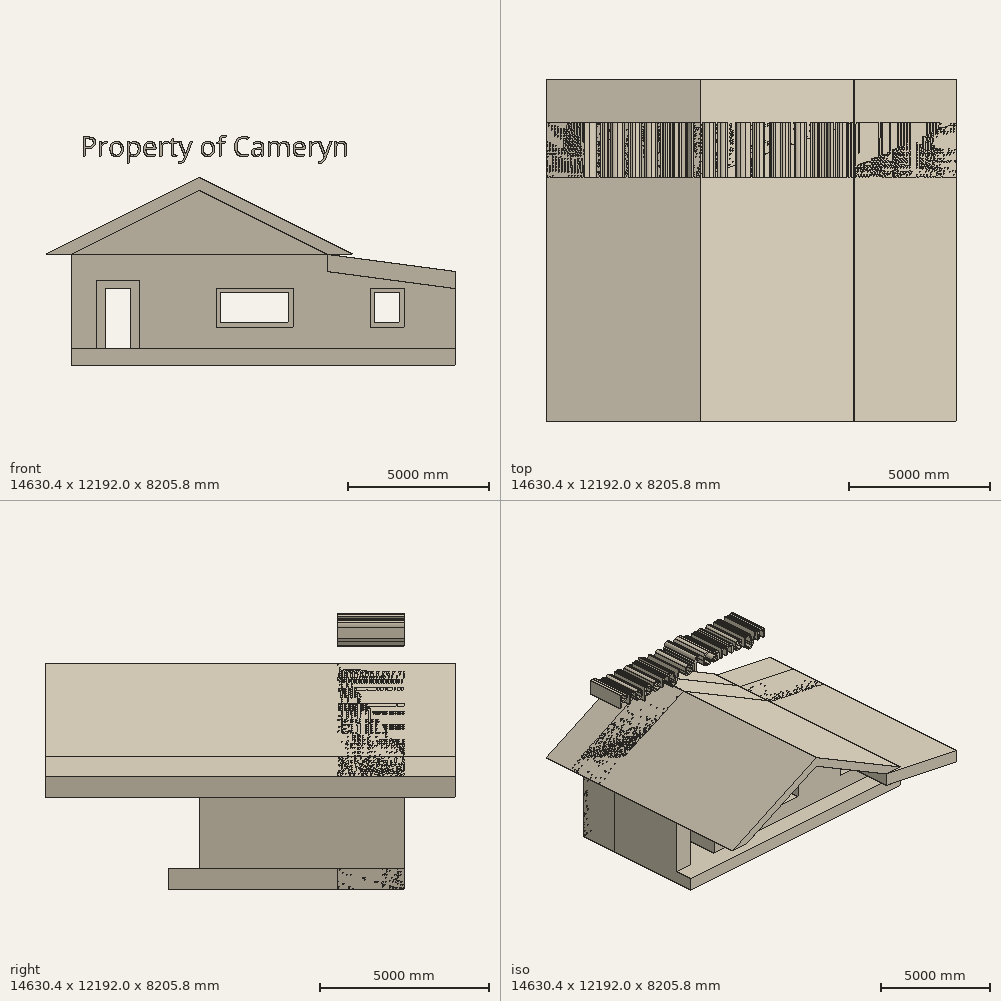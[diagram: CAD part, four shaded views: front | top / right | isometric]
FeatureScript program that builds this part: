
annotation { "Feature Type Name" : "Feature", "Feature Type Description" : "" }
export const myFeature = defineFeature(function(context is Context, id is Id, definition is map)
    precondition{}
    {
        {
            var Q0;
            Q0=qCreatedBy(makeId("Front.planeOp"),FACE);
            var sketch = newSketch(context, id + "F0", { "sketchPlane" : qUnion([Q0])});
            skLineSegment(sketch, "E0", {"start": v(0, 0) * mm, "end": v(-4572, 0) * mm});
            skLineSegment(sketch, "E1", {"start": v(0, 0) * mm, "end": v(4572, 0) * mm});
            skLineSegment(sketch, "E2", {"start": v(0, 0) * mm, "end": v(0, 2286) * mm});
            skLineSegment(sketch, "E3", {"start": v(0, 2286) * mm, "end": v(-4572, 0) * mm});
            skLineSegment(sketch, "E4", {"start": v(0, 2286) * mm, "end": v(4572, 0) * mm});
            skLineSegment(sketch, "E5", {"start": v(0, 2286) * mm, "end": v(0, 2743.2) * mm});
            skLineSegment(sketch, "E6", {"start": v(-4572, 0) * mm, "end": v(-5486.4, 0) * mm});
            skLineSegment(sketch, "E7", {"start": v(4572, 0) * mm, "end": v(5486.4, 0) * mm});
            skLineSegment(sketch, "E8", {"start": v(0, 2743.2) * mm, "end": v(5486.4, 0) * mm});
            skLineSegment(sketch, "E9", {"start": v(0, 2743.2) * mm, "end": v(-5486.4, 0) * mm});
            skLineSegment(sketch, "E10", {"start": v(-4572, 0) * mm, "end": v(-4572, -3352.8) * mm});
            skLineSegment(sketch, "E11", {"start": v(4572, 0) * mm, "end": v(4572, -3352.8) * mm});
            skLineSegment(sketch, "E12", {"start": v(-4572, -3352.8) * mm, "end": v(4572, -3352.8) * mm});
            skLineSegment(sketch, "E13", {"start": v(-4572, -3352.8) * mm, "end": v(-4572, -3962.4) * mm});
            skLineSegment(sketch, "E14", {"start": v(-4572, -3962.4) * mm, "end": v(4572, -3962.4) * mm});
            skLineSegment(sketch, "E15", {"start": v(4572, -3962.4) * mm, "end": v(4572, -3352.8) * mm});
            skLineSegment(sketch, "E16", {"start": v(4572, -3352.8) * mm, "end": v(9144, -3352.8) * mm});
            skLineSegment(sketch, "E17", {"start": v(4572, -3962.4) * mm, "end": v(9144, -3962.4) * mm});
            skLineSegment(sketch, "E18", {"start": v(9144, -3352.8) * mm, "end": v(9144, -3962.4) * mm});
            skLineSegment(sketch, "E19", {"start": v(4572, 0) * mm, "end": v(9143.16, -609.6) * mm});
            skLineSegment(sketch, "E20", {"start": v(9143.16, -609.6) * mm, "end": v(9144, -3352.8) * mm});
            skLineSegment(sketch, "E21", {"start": v(9143.16, -609.6) * mm, "end": v(9143.34, -1219.2) * mm});
            skLineSegment(sketch, "E22", {"start": v(9143.34, -1219.2) * mm, "end": v(4572, -609.6) * mm});
            skLineSegment(sketch, "E23", {"start": v(-3352.8, -3352.8) * mm, "end": v(-3352.8, -1219.2) * mm});
            skLineSegment(sketch, "E24", {"start": v(-3352.8, -1219.2) * mm, "end": v(-2438.4, -1219.2) * mm});
            skLineSegment(sketch, "E25", {"start": v(-2438.4, -1219.2) * mm, "end": v(-2438.4, -3352.8) * mm});
            skLineSegment(sketch, "E26.0", {"start": v(-2133.6, -914.4) * mm, "end": v(-2133.6, -3352.8) * mm});
            skLineSegment(sketch, "E26.1", {"start": v(-3657.6, -914.4) * mm, "end": v(-2133.6, -914.4) * mm});
            skLineSegment(sketch, "E26.2", {"start": v(-3657.6, -3352.8) * mm, "end": v(-3657.6, -914.4) * mm});
            skLineSegment(sketch, "E27", {"start": v(609.6, -1219.2) * mm, "end": v(609.6, -2590.8) * mm});
            skLineSegment(sketch, "E28", {"start": v(609.6, -1219.2) * mm, "end": v(3352.8, -1219.2) * mm});
            skLineSegment(sketch, "E29", {"start": v(3352.8, -1219.2) * mm, "end": v(3352.8, -2590.8) * mm});
            skLineSegment(sketch, "E30", {"start": v(3352.8, -2590.8) * mm, "end": v(609.6, -2590.8) * mm});
            skLineSegment(sketch, "E31.0", {"start": v(762, -1371.6) * mm, "end": v(3200.4, -1371.6) * mm});
            skLineSegment(sketch, "E31.1", {"start": v(762, -1371.6) * mm, "end": v(762, -2438.4) * mm});
            skLineSegment(sketch, "E31.2", {"start": v(3200.4, -2438.4) * mm, "end": v(762, -2438.4) * mm});
            skLineSegment(sketch, "E31.3", {"start": v(3200.4, -1371.6) * mm, "end": v(3200.4, -2438.4) * mm});
            skLineSegment(sketch, "E32", {"start": v(6096, -1219.2) * mm, "end": v(7315.2, -1219.2) * mm});
            skLineSegment(sketch, "E33", {"start": v(6096, -1219.2) * mm, "end": v(6096, -2590.8) * mm});
            skLineSegment(sketch, "E34", {"start": v(6096, -2590.8) * mm, "end": v(7315.2, -2590.8) * mm});
            skLineSegment(sketch, "E35", {"start": v(7315.2, -2590.8) * mm, "end": v(7315.2, -1219.2) * mm});
            skLineSegment(sketch, "E36.0", {"start": v(6248.4, -1371.6) * mm, "end": v(7162.8, -1371.6) * mm});
            skLineSegment(sketch, "E36.1", {"start": v(6248.4, -1371.6) * mm, "end": v(6248.4, -2438.4) * mm});
            skLineSegment(sketch, "E36.2", {"start": v(6248.4, -2438.4) * mm, "end": v(7162.8, -2438.4) * mm});
            skLineSegment(sketch, "E36.3", {"start": v(7162.8, -2438.4) * mm, "end": v(7162.8, -1371.6) * mm});
            skText(sketch, "E37", { "text": "Property of Cameryn", "fontName": "OpenSans-Regular.ttf"});
            const initialGuessF0  = {"E37": [-4.24079, 3.48834, 1, 0, 0.71045]};
            skSetInitialGuess(sketch, initialGuessF0);
            skSolve(sketch);
        }
        {
            var Q0;
            Q0=makeQuery(id+"F0.imprint","IMPRINT",FACE,{"disambiguationData":[TD([[makeQuery(id+"F0.imprint","IMPRINT",EDGE,{"derivedFrom":sQuery(id+"F0.wireOp",EDGE,"E4")}),1.0]])]});
            var Q1;
            Q1=makeQuery(id+"F0.imprint","IMPRINT",FACE,{"disambiguationData":[TD([[makeQuery(id+"F0.imprint","IMPRINT",EDGE,{"derivedFrom":sQuery(id+"F0.wireOp",EDGE,"E3")}),-1.0]])]});
            var Q2;
            {var subQ0=sQuery(id+"F0.wireOp",EDGE,"E19");Q2=makeQuery(id+"F0.imprint","IMPRINT",FACE,{"disambiguationData":[TD([[makeQuery(id+"F0.imprint","IMPRINT",EDGE,{"derivedFrom":subQ0}),-1.0]])]});}
            extrude(context, id + "F1", {"entities" : qUnion([Q0, Q1, Q2]), "depth" : 10668 * mm, "offsetDistance" : 30.48 * mm, "hasSecondDirection" : true, "secondDirectionOppositeDirection" : true, "secondDirectionDepth" : 1524 * mm});
        }
        {
            var Q0;
            Q0=makeQuery(id+"F0.imprint","IMPRINT",FACE,{"disambiguationData":[TD([[makeQuery(id+"F0.imprint","IMPRINT",EDGE,{"derivedFrom":sQuery(id+"F0.wireOp",EDGE,"E0")}),-1.0]])]});
            var Q1;
            Q1=makeQuery(id+"F0.imprint","IMPRINT",FACE,{"disambiguationData":[TD([[makeQuery(id+"F0.imprint","IMPRINT",EDGE,{"derivedFrom":sQuery(id+"F0.wireOp",EDGE,"E1")}),1.0]])]});
            extrude(context, id + "F2", {"entities" : qUnion([Q0, Q1]), "operationType" : NewBodyOperationType.ADD, "depth" : 1524 * mm, "offsetDistance" : 30.48 * mm, "hasSecondDirection" : true, "secondDirectionOppositeDirection" : true, "secondDirectionDepth" : 1524 * mm});
        }
        {
            var Q0;
            Q0=makeQuery(id+"F0.imprint","IMPRINT",FACE,{"disambiguationData":[TD([[makeQuery(id+"F0.imprint","IMPRINT",EDGE,{"derivedFrom":sQuery(id+"F0.wireOp",EDGE,"E0")}),1.0]])]});
            var Q1;
            {var subQ0=sQuery(id+"F0.wireOp",EDGE,"E16");Q1=makeQuery(id+"F0.imprint","IMPRINT",FACE,{"disambiguationData":[TD([[makeQuery(id+"F0.imprint","IMPRINT",EDGE,{"derivedFrom":subQ0}),1.0]])]});}
            extrude(context, id + "F3", {"entities" : qUnion([Q0, Q1]), "depth" : 6096 * mm, "offsetDistance" : 30.48 * mm});
        }
        {
            var Q0;
            {var subQ5=sQuery(id+"F0.wireOp",EDGE,"E13");Q0=makeQuery(id+"F0.imprint","IMPRINT",FACE,{"disambiguationData":[TD([[makeQuery(id+"F0.imprint","IMPRINT",EDGE,{"derivedFrom":subQ5}),1.0]])]});}
            var Q1;
            Q1=makeQuery(id+"F0.imprint","IMPRINT",FACE,{"disambiguationData":[TD([[makeQuery(id+"F0.imprint","IMPRINT",EDGE,{"derivedFrom":sQuery(id+"F0.wireOp",EDGE,"E15")}),-1.0]])]});
            extrude(context, id + "F4", {"entities" : qUnion([Q0, Q1]), "operationType" : NewBodyOperationType.ADD, "depth" : 7010.4 * mm, "offsetDistance" : 30.48 * mm});
        }
        {
            var Q0;
            {var subQ0=sQuery(id+"F0.wireOp",EDGE,"E23");Q0=makeQuery(id+"F0.imprint","IMPRINT",FACE,{"disambiguationData":[TD([[makeQuery(id+"F0.imprint","IMPRINT",EDGE,{"derivedFrom":subQ0}),1.0]])]});}
            var Q1;
            Q1=makeQuery(id+"F0.imprint","IMPRINT",FACE,{"disambiguationData":[TD([[makeQuery(id+"F0.imprint","IMPRINT",EDGE,{"derivedFrom":sQuery(id+"F0.wireOp",EDGE,"E27")}),1.0]])]});
            var Q2;
            Q2=makeQuery(id+"F0.imprint","IMPRINT",FACE,{"disambiguationData":[TD([[makeQuery(id+"F0.imprint","IMPRINT",EDGE,{"derivedFrom":sQuery(id+"F0.wireOp",EDGE,"E32")}),-1.0]])]});
            extrude(context, id + "F5", {"entities" : qUnion([Q0, Q1, Q2]), "operationType" : NewBodyOperationType.ADD, "depth" : 609.6 * mm, "offsetDistance" : 30.48 * mm});
        }
        {
            var Q0;
            Q0 = qSketchRegion(id + "F0", true);
            extrude(context, id + "F6", {"entities" : qUnion([Q0]), "depth" : 1981.2 * mm, "offsetDistance" : 30.48 * mm});
        }
    });
